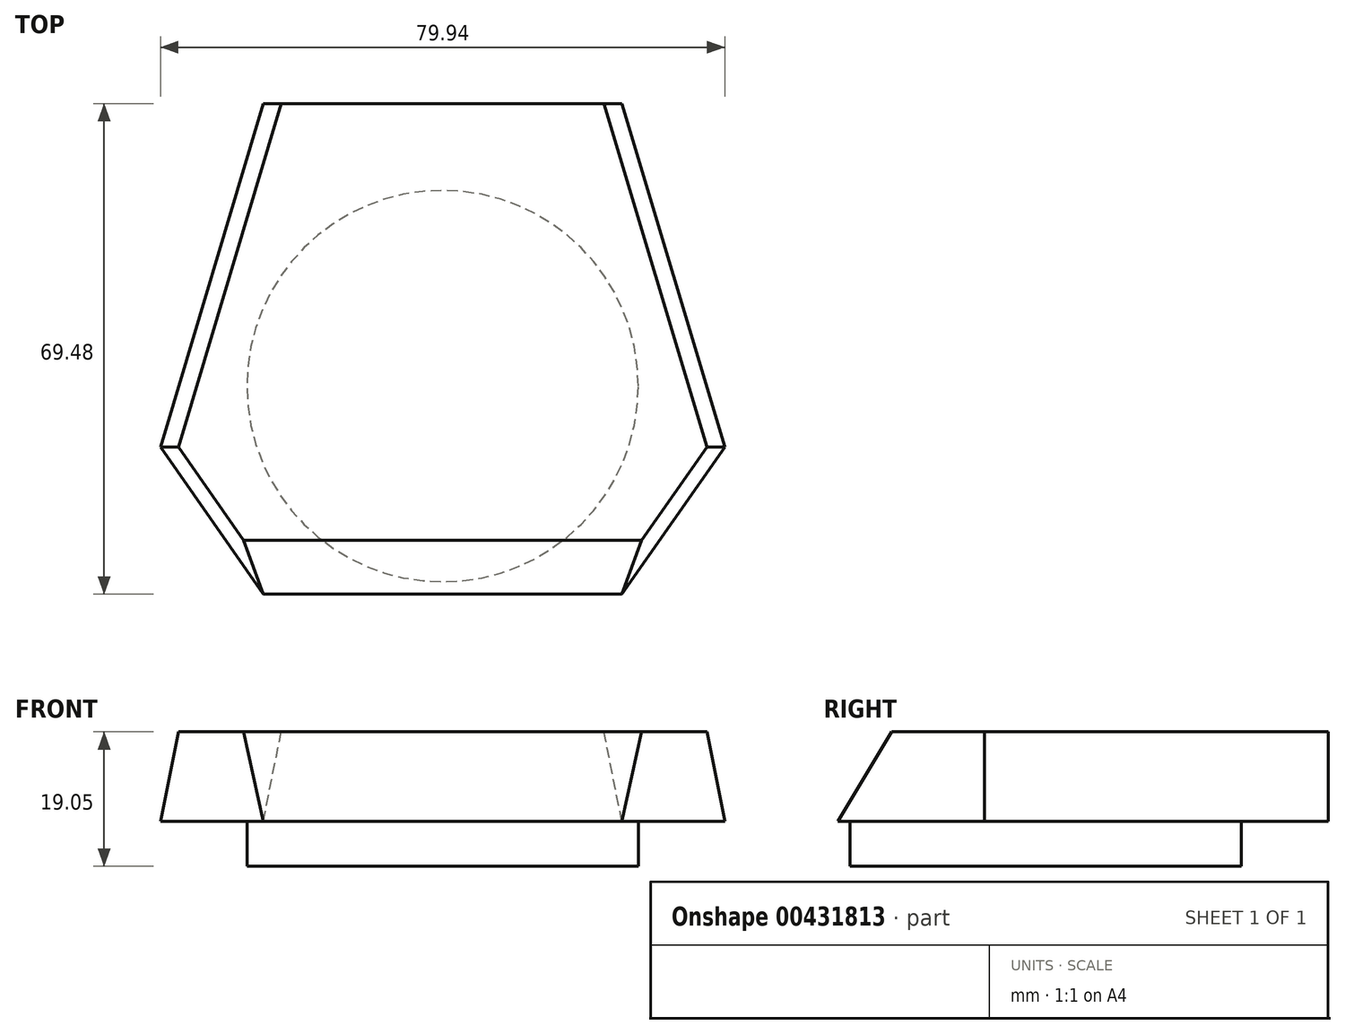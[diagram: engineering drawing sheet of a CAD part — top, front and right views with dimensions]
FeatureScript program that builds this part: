
annotation { "Feature Type Name" : "Feature", "Feature Type Description" : "" }
export const myFeature = defineFeature(function(context is Context, id is Id, definition is map)
    precondition{}
    {
        {
            var Q0;
            Q0=qCreatedBy(makeId("Top.planeOp"),FACE);
            var sketch = newSketch(context, id + "F0", { "sketchPlane" : qUnion([Q0])});
            skLineSegment(sketch, "E0", {"start": v(0, -20.8) * mm, "end": v(25.4, -20.8) * mm});
            skLineSegment(sketch, "E1", {"start": v(25.4, -20.8) * mm, "end": v(39.97, 0) * mm});
            skLineSegment(sketch, "E2", {"start": v(39.97, 0) * mm, "end": v(25.4, 48.67) * mm});
            skLineSegment(sketch, "E3", {"start": v(25.4, 48.67) * mm, "end": v(0, 48.67) * mm});
            skLineSegment(sketch, "E4", {"start": v(0, 48.67) * mm, "end": v(-25.4, 48.67) * mm});
            skLineSegment(sketch, "E5", {"start": v(0, -20.8) * mm, "end": v(-25.4, -20.8) * mm});
            skLineSegment(sketch, "E6", {"start": v(-25.4, -20.8) * mm, "end": v(-39.97, 0) * mm});
            skLineSegment(sketch, "E7", {"start": v(-39.97, 0) * mm, "end": v(-25.4, 48.67) * mm});
            skSolve(sketch);
        }
        {
            var Q0;
            Q0=makeQuery(id+"F0.imprint","IMPRINT",FACE,{"disambiguationData":[TD([[makeQuery(id+"F0.imprint","IMPRINT",EDGE,{"derivedFrom":sQuery(id+"F0.wireOp",EDGE,"E0")}),1.0]])]});
            cPlane(context, id + "F1", {"entities" : qUnion([Q0]), "cplaneType" : CPlaneType.OFFSET, "offset" : 12.7 * mm, "width" : 152.4 * mm, "height" : 152.4 * mm});
        }
        {
            var Q0;
            Q0=qCreatedBy(id+"F1.planeOp",FACE);
            var sketch = newSketch(context, id + "F2", { "sketchPlane" : qUnion([Q0])});
            skLineSegment(sketch, "E8", {"start": v(0, 48.67) * mm, "end": v(-22.86, 48.67) * mm});
            skLineSegment(sketch, "E9", {"start": v(0, 48.67) * mm, "end": v(22.86, 48.67) * mm});
            skLineSegment(sketch, "E10", {"start": v(-22.86, 48.67) * mm, "end": v(-37.43, 0) * mm});
            skLineSegment(sketch, "E11", {"start": v(-37.43, 0) * mm, "end": v(-28.2, -13.19) * mm});
            skLineSegment(sketch, "E12", {"start": v(0, -13.19) * mm, "end": v(-28.2, -13.19) * mm});
            skLineSegment(sketch, "E13", {"start": v(0, -13.19) * mm, "end": v(28.2, -13.19) * mm});
            skLineSegment(sketch, "E14", {"start": v(28.2, -13.19) * mm, "end": v(37.43, 0) * mm});
            skLineSegment(sketch, "E15", {"start": v(22.86, 48.67) * mm, "end": v(37.43, 0) * mm});
            skSolve(sketch);
        }
        {
            var Q0;
            Q0=makeQuery(id+"F0.imprint","IMPRINT",FACE,{"disambiguationData":[TD([[makeQuery(id+"F0.imprint","IMPRINT",EDGE,{"derivedFrom":sQuery(id+"F0.wireOp",EDGE,"E0")}),1.0]])]});
            var Q1;
            Q1=makeQuery(id+"F2.imprint","IMPRINT",FACE,{"disambiguationData":[TD([[makeQuery(id+"F2.imprint","IMPRINT",EDGE,{"derivedFrom":sQuery(id+"F2.wireOp",EDGE,"E8")}),1.0]])]});
            loft(context, id + "F3", {"sheetProfilesArray" : [{ "sheetProfileEntities" : qUnion([Q0]) }, { "sheetProfileEntities" : qUnion([Q1]) }]});
        }
        {
            var Q0;
            Q0=makeQuery(id+"F3.opLoft","CAP_FACE",FACE,{"disambiguationData":[OSD([makeQuery(id+"F0.imprint","IMPRINT",FACE,{"disambiguationData":[TD([[makeQuery(id+"F0.imprint","IMPRINT",EDGE,{"derivedFrom":sQuery(id+"F0.wireOp",EDGE,"E0")}),1.0]])]})])],"isStart":true});
            var sketch = newSketch(context, id + "F4", { "sketchPlane" : qUnion([Q0])});
            skCircle(sketch, "E16", {"center": v(0, -8.66) * mm, "radius": 27.72 * mm});
            skSolve(sketch);
        }
        {
            var Q0;
            Q0=makeQuery(id+"F4.imprint","IMPRINT",FACE,{"disambiguationData":[TD([[makeQuery(id+"F4.imprint","IMPRINT",EDGE,{"derivedFrom":sQuery(id+"F4.wireOp",EDGE,"E16")}),1.0]])]});
            extrude(context, id + "F5", {"entities" : qUnion([Q0]), "operationType" : NewBodyOperationType.ADD, "depth" : 6.35 * mm});
        }
    });
